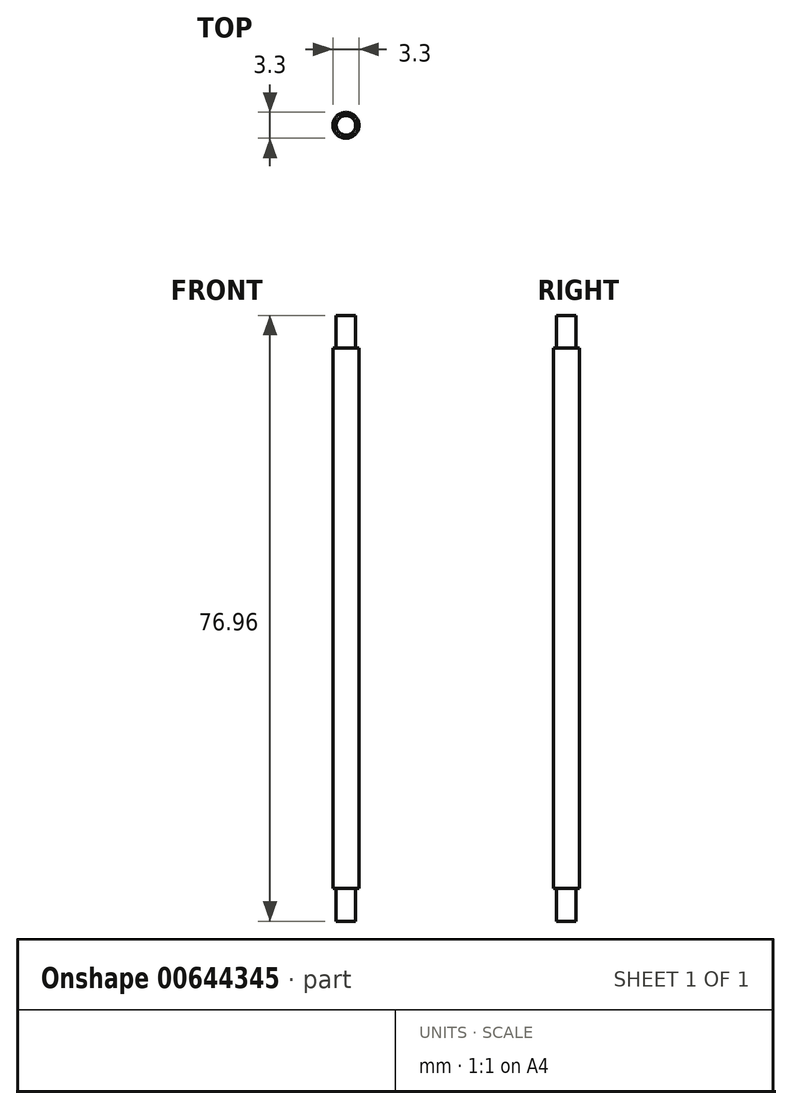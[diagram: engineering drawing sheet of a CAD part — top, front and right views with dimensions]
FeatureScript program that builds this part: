
annotation { "Feature Type Name" : "Feature", "Feature Type Description" : "" }
export const myFeature = defineFeature(function(context is Context, id is Id, definition is map)
    precondition{}
    {
        {
            var Q0;
            Q0=qCreatedBy(makeId("Front.planeOp"),FACE);
            var sketch = newSketch(context, id + "F0", { "sketchPlane" : qUnion([Q0])});
            skLineSegment(sketch, "E0", {"start": v(-54.15, 38.75) * mm, "end": v(-54.15, -29.88) * mm});
            skLineSegment(sketch, "E1", {"start": v(-54.15, 38.75) * mm, "end": v(-53.74, 38.75) * mm});
            skLineSegment(sketch, "E2", {"start": v(-53.74, 38.75) * mm, "end": v(-53.74, 42.91) * mm});
            skLineSegment(sketch, "E3", {"start": v(-53.74, 42.91) * mm, "end": v(-52.5, 42.91) * mm});
            skLineSegment(sketch, "E4", {"start": v(-52.5, 42.91) * mm, "end": v(-52.5, -34.05) * mm});
            skLineSegment(sketch, "E5", {"start": v(-54.15, -29.88) * mm, "end": v(-53.74, -29.88) * mm});
            skLineSegment(sketch, "E6", {"start": v(-53.74, -29.88) * mm, "end": v(-53.74, -34.05) * mm});
            skLineSegment(sketch, "E7", {"start": v(-53.74, -34.05) * mm, "end": v(-52.5, -34.05) * mm});
            skSolve(sketch);
        }
        {
            var Q0;
            Q0 = qSketchRegion(id + "F0", true);
            var Q1;
            Q1=sQuery(id+"F0.wireOp",EDGE,"E4");
            revolve(context, id + "F1", {"entities" : qUnion([Q0]), "axis" : qUnion([Q1]), "revolveType" : RevolveType.FULL});
        }
    });
